# Revit family: 2-5146-224 Chameleon
name_source: partatom
category: Lighting Fixtures
revit_build: Autodesk Revit LT 2014 (Build: 20130308_1515(x64)
units: mm (PartAtom-declared; Revit-internal decimal feet)

## types (1)
- 2-5146-224 Chameleon
    ADA Compliant = Yes
    Acrylic = Acrylic Matte White
    Apparent Load = 29 VA
    Ballast Manufacuturer = Fulham
    Color Filter = 16777215
    Default Elevation = 4' - 0"
    Description = 11" Wall Sconce- 2x Twin tube compact fluorescent
    Dimming Lamp Color Temperature Shift = <None>
    Emit Shape Visible in Rendering = No
    Emit from Rectangle Length = 4' - 0"
    Emit from Rectangle Width = 2' - 0"
    Fixture Depth = 0' - 4"
    Fixture Height = 0' - 10 15/16"
    Fixture Width = 0' - 11 7/16"
    Input Power (Watts) = 28.80
    Input Voltage (Volts AC) = 120.0
    Junction Box = 4" Octogonal
    Lamp = 2X13W Twin Tube Compact Fluorescents
    Lamp Manufacturer = Sylvania
    Manufacturer = Oxygen Lighting
    Metal Finish = Satin Nickel
    Model = 2-5146-224
    Photometric Web File = 2-5146-224 Chameleon ITL77188.IES
    Power Factor = 0.99
    Product Documentation Link = http://oxygenlighting.com.s3.amazonaws.com
    Tilt Angle = 180.00°
    Type Comments = Lighting - Fluorescent
    URL = http://www.oxygenlighting.com

## geometry (parser evidence)
native form markers: Sweep x1
no freeform markers — native parametric forms only
